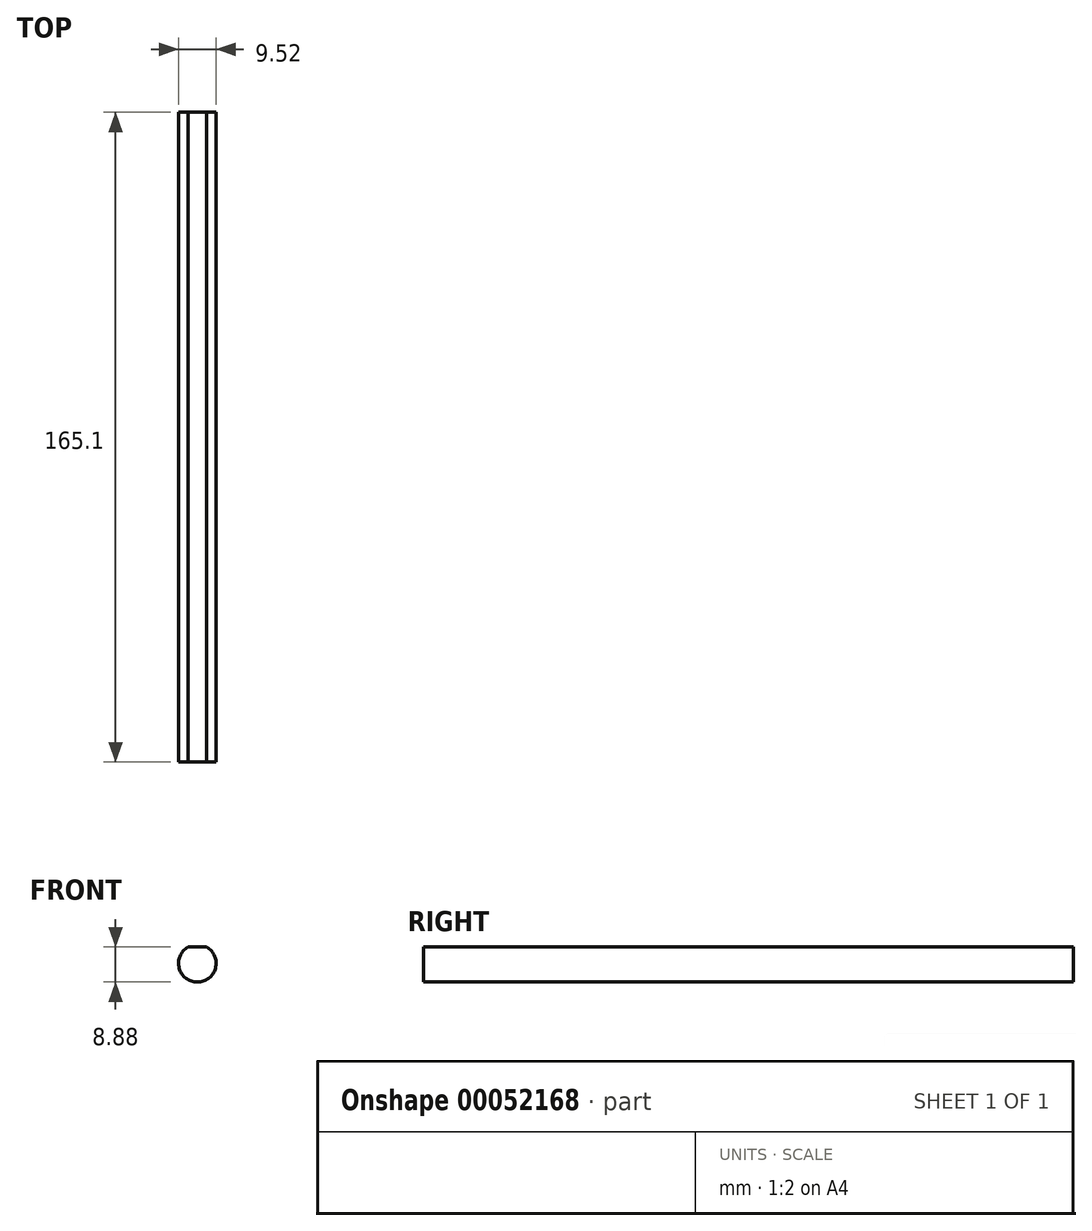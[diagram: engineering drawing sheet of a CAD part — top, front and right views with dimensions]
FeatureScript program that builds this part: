
annotation { "Feature Type Name" : "Feature", "Feature Type Description" : "" }
export const myFeature = defineFeature(function(context is Context, id is Id, definition is map)
    precondition{}
    {
        {
            var Q0;
            Q0=qCreatedBy(makeId("Front.planeOp"),FACE);
            var sketch = newSketch(context, id + "F0", { "sketchPlane" : qUnion([Q0])});
            skArc(sketch, "E0", {"start": v(-2.39, 4.12) * mm, "mid": v(0, -4.76) * mm, "end": v(2.39, 4.12) * mm});
            skLineSegment(sketch, "E1", {"start": v(-2.39, 4.12) * mm, "end": v(2.39, 4.12) * mm});
            skSolve(sketch);
        }
        {
            var Q0;
            Q0=makeQuery(id+"F0.imprint","IMPRINT",FACE,{"disambiguationData":[TD([[makeQuery(id+"F0.imprint","IMPRINT",EDGE,{"derivedFrom":sQuery(id+"F0.wireOp",EDGE,"E0")}),1.0]])]});
            extrude(context, id + "F1", {"entities" : qUnion([Q0]), "endBound" : BoundingType.SYMMETRIC, "depth" : 165.1 * mm});
        }
    });
